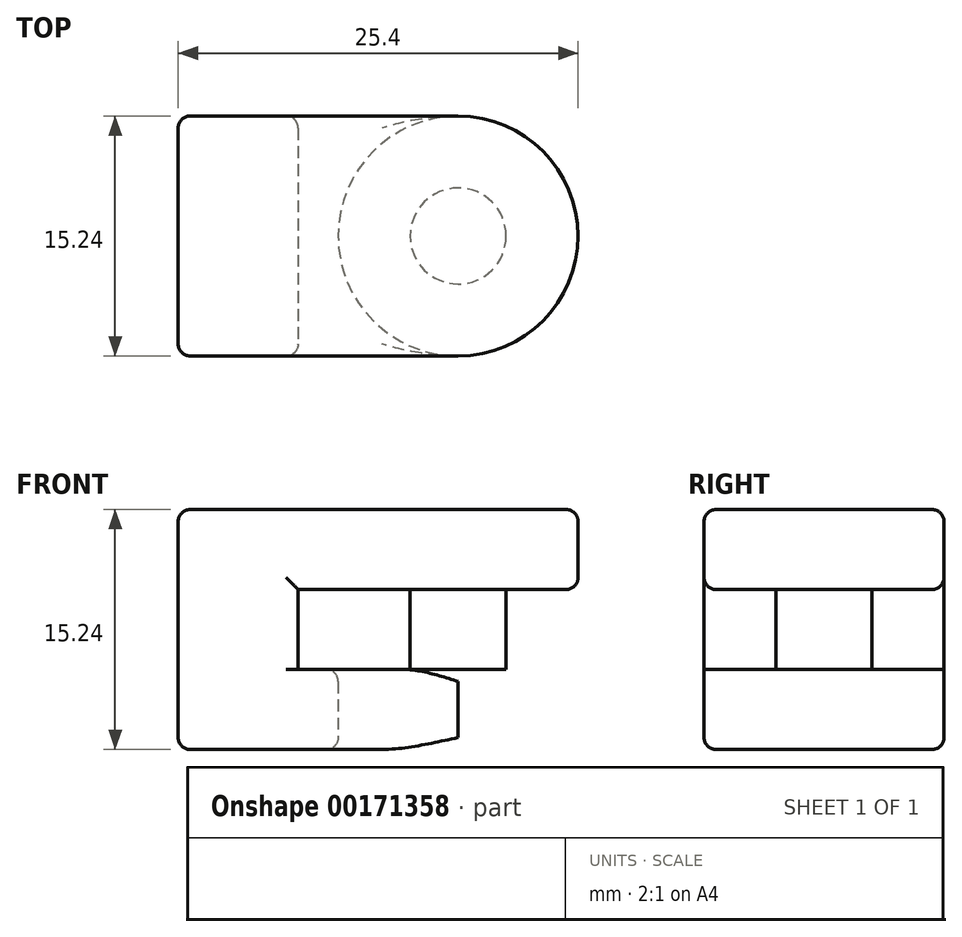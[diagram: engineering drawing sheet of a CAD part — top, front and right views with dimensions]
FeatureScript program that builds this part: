
annotation { "Feature Type Name" : "Feature", "Feature Type Description" : "" }
export const myFeature = defineFeature(function(context is Context, id is Id, definition is map)
    precondition{}
    {
        {
            var Q0;
            Q0=qCreatedBy(makeId("Top.planeOp"),FACE);
            var sketch = newSketch(context, id + "F0", { "sketchPlane" : qUnion([Q0])});
            skCircle(sketch, "E0", {"center": v(0, 0) * mm, "radius": 7.62 * mm});
            skLineSegment(sketch, "E1.bottom", {"start": v(0, 7.62) * mm, "end": v(-17.78, 7.62) * mm});
            skLineSegment(sketch, "E1.top", {"start": v(0, -7.62) * mm, "end": v(-17.78, -7.62) * mm});
            skLineSegment(sketch, "E1.left", {"start": v(0, 7.62) * mm, "end": v(0, -7.62) * mm});
            skLineSegment(sketch, "E1.right", {"start": v(-17.78, 7.62) * mm, "end": v(-17.78, -7.62) * mm});
            skLineSegment(sketch, "E2.bottom", {"start": v(0, -7.62) * mm, "end": v(0, -7.62) * mm});
            skLineSegment(sketch, "E2.top", {"start": v(0, 7.62) * mm, "end": v(0, 7.62) * mm});
            skLineSegment(sketch, "E2.right", {"start": v(0, -7.62) * mm, "end": v(0, 7.62) * mm});
            skSolve(sketch);
        }
        {
            var Q0;
            {var subQ1=sQuery(id+"F0.wireOp",EDGE,"E1.bottom");Q0=makeQuery(id+"F0.imprint","IMPRINT",FACE,{"disambiguationData":[TD([[makeQuery(id+"F0.imprint","IMPRINT",EDGE,{"derivedFrom":subQ1}),1.0]])]});}
            var Q1;
            {var subQ0=sQuery(id+"F0.wireOp",EDGE,"E2.right");Q1=makeQuery(id+"F0.imprint","IMPRINT",FACE,{"disambiguationData":[TD([[makeQuery(id+"F0.imprint","IMPRINT",EDGE,{"derivedFrom":subQ0}),1.0]])]});}
            var Q2;
            {var subQ0=sQuery(id+"F0.wireOp",EDGE,"E2.right");Q2=makeQuery(id+"F0.imprint","IMPRINT",FACE,{"disambiguationData":[TD([[makeQuery(id+"F0.imprint","IMPRINT",EDGE,{"derivedFrom":subQ0}),-1.0]])]});}
            extrude(context, id + "F1", {"entities" : qUnion([Q0, Q1, Q2]), "depth" : 5.08 * mm});
        }
        {
            var Q0;
            Q0=makeQuery(id+"F1.opExtrude","CAP_FACE",FACE,{"disambiguationData":[OSD([sQuery(id+"F0.wireOp",EDGE,"E0"),sQuery(id+"F0.wireOp",EDGE,"E1.bottom"),sQuery(id+"F0.wireOp",EDGE,"E1.top"),sQuery(id+"F0.wireOp",EDGE,"E1.right")])],"isStart":false});
            var sketch = newSketch(context, id + "F2", { "sketchPlane" : qUnion([Q0])});
            skCircle(sketch, "E3", {"center": v(0, 0) * mm, "radius": 3.05 * mm});
            skSolve(sketch);
        }
        {
            var Q0;
            Q0 = qSketchRegion(id + "F2", true);
            var Q1;
            Q1 = qSketchRegion(id + "F4", true);
            extrude(context, id + "F3", {"entities" : qUnion([Q0, Q1]), "operationType" : NewBodyOperationType.ADD, "depth" : 5.08 * mm});
        }
        {
            var Q0;
            Q0=makeQuery(id+"F3.opExtrude","CAP_FACE",FACE,{"disambiguationData":[OSD([sQuery(id+"F2.wireOp",EDGE,"E3")])],"isStart":false});
            var sketch = newSketch(context, id + "F4", { "sketchPlane" : qUnion([Q0])});
            skCircle(sketch, "E4", {"center": v(0, 0) * mm, "radius": 7.62 * mm});
            skLineSegment(sketch, "E5.bottom", {"start": v(0, 7.62) * mm, "end": v(-17.78, 7.62) * mm});
            skLineSegment(sketch, "E5.top", {"start": v(0, -7.62) * mm, "end": v(-17.78, -7.62) * mm});
            skLineSegment(sketch, "E5.left", {"start": v(0, 7.62) * mm, "end": v(0, -7.62) * mm});
            skLineSegment(sketch, "E5.right", {"start": v(-17.78, 7.62) * mm, "end": v(-17.78, -7.62) * mm});
            skLineSegment(sketch, "E6.bottom", {"start": v(0, -7.62) * mm, "end": v(0, -7.62) * mm});
            skLineSegment(sketch, "E6.top", {"start": v(0, 7.62) * mm, "end": v(0, 7.62) * mm});
            skLineSegment(sketch, "E6.right", {"start": v(0, -7.62) * mm, "end": v(0, 7.62) * mm});
            skSolve(sketch);
        }
        {
            var Q0;
            {var subQ0=sQuery(id+"F4.wireOp",EDGE,"E6.right");var subQ1=makeQuery(id+"F3.opExtrude","CAP_EDGE",EDGE,{"disambiguationData":[OSD([sQuery(id+"F2.wireOp",EDGE,"E3")])],"isStart":false});var subQ2=makeQuery(id+"F4.imprint","INTERSECT",VERTEX,{"disambiguationData":[OD(0.0)],"derivedFrom":[subQ1,subQ0]});Q0=makeQuery(id+"F4.imprint","IMPRINT",FACE,{"disambiguationData":[TD([[makeQuery(id+"F4.imprint","IMPRINT",EDGE,{"disambiguationData":[TD([[subQ2,-1.0]])],"derivedFrom":subQ0}),1.0]])]});}
            var Q1;
            {var subQ0=sQuery(id+"F4.wireOp",EDGE,"E6.right");var subQ1=makeQuery(id+"F3.opExtrude","CAP_EDGE",EDGE,{"disambiguationData":[OSD([sQuery(id+"F2.wireOp",EDGE,"E3")])],"isStart":false});var subQ2=makeQuery(id+"F4.imprint","INTERSECT",VERTEX,{"disambiguationData":[OD(0.0)],"derivedFrom":[subQ1,subQ0]});Q1=makeQuery(id+"F4.imprint","IMPRINT",FACE,{"disambiguationData":[TD([[makeQuery(id+"F4.imprint","IMPRINT",EDGE,{"disambiguationData":[TD([[subQ2,-1.0]])],"derivedFrom":subQ0}),-1.0]])]});}
            var Q2;
            {var subQ1=sQuery(id+"F4.wireOp",EDGE,"E5.bottom");Q2=makeQuery(id+"F4.imprint","IMPRINT",FACE,{"disambiguationData":[TD([[makeQuery(id+"F4.imprint","IMPRINT",EDGE,{"derivedFrom":subQ1}),1.0]])]});}
            var Q3;
            Q3 = qSketchRegion(id + "F4", true);
            extrude(context, id + "F5", {"entities" : qUnion([Q0, Q1, Q2, Q3]), "operationType" : NewBodyOperationType.ADD, "depth" : 5.08 * mm});
        }
        {
            var Q0;
            Q0=makeQuery(id+"F1.opExtrude","CAP_FACE",FACE,{"disambiguationData":[OSD([sQuery(id+"F0.wireOp",EDGE,"E0"),sQuery(id+"F0.wireOp",EDGE,"E1.bottom"),sQuery(id+"F0.wireOp",EDGE,"E1.top"),sQuery(id+"F0.wireOp",EDGE,"E1.right")])],"isStart":false});
            var sketch = newSketch(context, id + "F6", { "sketchPlane" : qUnion([Q0])});
            skLineSegment(sketch, "E7.bottom", {"start": v(-17.78, 7.62) * mm, "end": v(-10.16, 7.62) * mm});
            skLineSegment(sketch, "E7.top", {"start": v(-17.78, -7.62) * mm, "end": v(-10.16, -7.62) * mm});
            skLineSegment(sketch, "E7.left", {"start": v(-17.78, 7.62) * mm, "end": v(-17.78, -7.62) * mm});
            skLineSegment(sketch, "E7.right", {"start": v(-10.16, 7.62) * mm, "end": v(-10.16, -7.62) * mm});
            skSolve(sketch);
        }
        {
            var Q0;
            Q0=makeQuery(id+"F6.imprint","IMPRINT",FACE,{"disambiguationData":[TD([[makeQuery(id+"F6.imprint","IMPRINT",EDGE,{"derivedFrom":sQuery(id+"F6.wireOp",EDGE,"E7.bottom")}),1.0]])]});
            extrude(context, id + "F7", {"entities" : qUnion([Q0]), "operationType" : NewBodyOperationType.ADD, "depth" : 5.08 * mm});
        }
        {
            var Q0;
            Q0=makeQuery(id+"F1.opExtrude","CAP_EDGE",EDGE,{"disambiguationData":[OSD([sQuery(id+"F0.wireOp",EDGE,"E1.bottom")])],"isStart":true});
            var Q1;
            Q1=makeQuery(id+"F1.opExtrude","CAP_EDGE",EDGE,{"disambiguationData":[OSD([sQuery(id+"F0.wireOp",EDGE,"E0")])],"isStart":true});
            var Q2;
            Q2=makeQuery(id+"F1.opExtrude","CAP_EDGE",EDGE,{"disambiguationData":[OSD([sQuery(id+"F0.wireOp",EDGE,"E1.top")])],"isStart":true});
            var Q3;
            Q3=makeQuery(id+"F5.opExtrude","CAP_EDGE",EDGE,{"disambiguationData":[OSD([sQuery(id+"F4.wireOp",EDGE,"E4")])],"isStart":false});
            var Q4;
            Q4=makeQuery(id+"F7.boolean.opBoolean","MERGE",EDGE,{"derivedFrom":[makeQuery(id+"F1.opExtrude","SWEPT_EDGE",EDGE,{"disambiguationData":[OSD([sQuery(id+"F0.wireOp",EDGE,"E1.bottom"),sQuery(id+"F0.wireOp",EDGE,"E1.right")])]}),makeQuery(id+"F5.opExtrude","SWEPT_EDGE",EDGE,{"disambiguationData":[OSD([sQuery(id+"F4.wireOp",EDGE,"E5.bottom"),sQuery(id+"F4.wireOp",EDGE,"E5.right")])]}),makeQuery(id+"F7.opExtrude","SWEPT_EDGE",EDGE,{"disambiguationData":[OSD([sQuery(id+"F6.wireOp",EDGE,"E7.bottom"),sQuery(id+"F6.wireOp",EDGE,"E7.left")])]})]});
            var Q5;
            Q5=makeQuery(id+"F1.opExtrude","CAP_EDGE",EDGE,{"disambiguationData":[OSD([sQuery(id+"F0.wireOp",EDGE,"E1.right")])],"isStart":true});
            var Q6;
            Q6=makeQuery(id+"F7.boolean.opBoolean","MERGE",EDGE,{"derivedFrom":[makeQuery(id+"F1.opExtrude","SWEPT_EDGE",EDGE,{"disambiguationData":[OSD([sQuery(id+"F0.wireOp",EDGE,"E1.top"),sQuery(id+"F0.wireOp",EDGE,"E1.right")])]}),makeQuery(id+"F5.opExtrude","SWEPT_EDGE",EDGE,{"disambiguationData":[OSD([sQuery(id+"F4.wireOp",EDGE,"E5.top"),sQuery(id+"F4.wireOp",EDGE,"E5.right")])]}),makeQuery(id+"F7.opExtrude","SWEPT_EDGE",EDGE,{"disambiguationData":[OSD([sQuery(id+"F6.wireOp",EDGE,"E7.top"),sQuery(id+"F6.wireOp",EDGE,"E7.left")])]})]});
            var Q7;
            Q7=makeQuery(id+"F5.opExtrude","CAP_EDGE",EDGE,{"disambiguationData":[OSD([sQuery(id+"F4.wireOp",EDGE,"E5.right")])],"isStart":false});
            var Q8;
            Q8=makeQuery(id+"F1.opExtrude","CAP_EDGE",EDGE,{"disambiguationData":[OSD([sQuery(id+"F0.wireOp",EDGE,"E0")])],"isStart":false});
            var Q9;
            Q9=makeQuery(id+"F5.opExtrude","CAP_EDGE",EDGE,{"disambiguationData":[OSD([sQuery(id+"F4.wireOp",EDGE,"E4")])],"isStart":true});
            var Q10;
            Q10=makeQuery(id+"F7.opExtrude","SWEPT_EDGE",EDGE,{"disambiguationData":[OSD([sQuery(id+"F0.wireOp",EDGE,"E1.top"),sQuery(id+"F6.wireOp",EDGE,"E7.top"),sQuery(id+"F6.wireOp",EDGE,"E7.right")])]});
            var Q11;
            Q11=makeQuery(id+"F7.opExtrude","SWEPT_EDGE",EDGE,{"disambiguationData":[OSD([sQuery(id+"F0.wireOp",EDGE,"E1.bottom"),sQuery(id+"F6.wireOp",EDGE,"E7.bottom"),sQuery(id+"F6.wireOp",EDGE,"E7.right")])]});
            fillet(context, id + "F8", {"entities" : qUnion([Q0, Q1, Q2, Q3, Q4, Q5, Q6, Q7, Q8, Q9, Q10, Q11]), "radius" : 0.76 * mm, "tangentPropagation" : true, "allowEdgeOverflow" : false});
        }
    });
